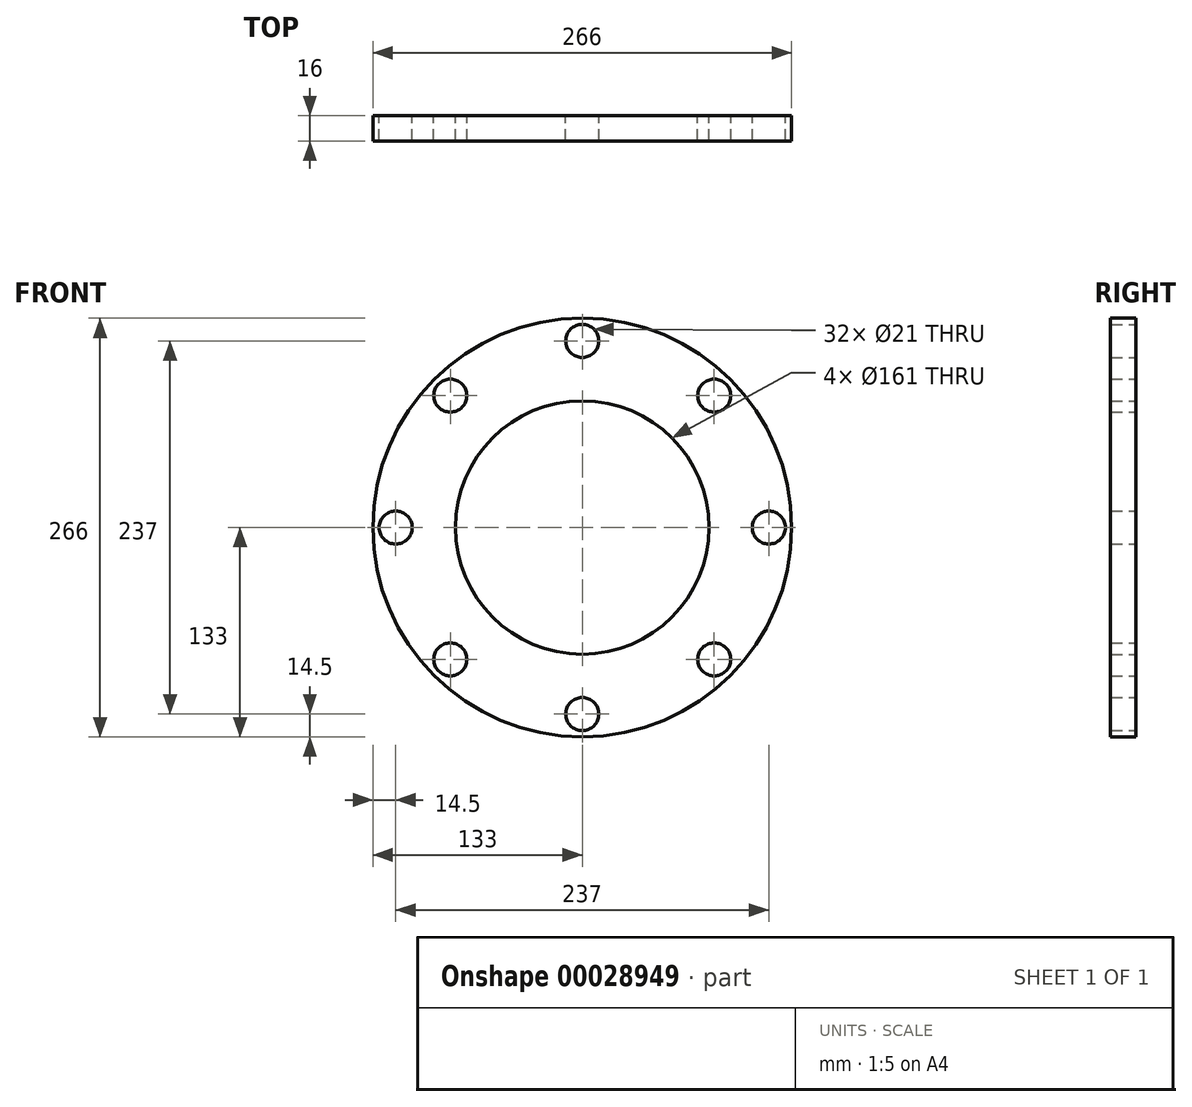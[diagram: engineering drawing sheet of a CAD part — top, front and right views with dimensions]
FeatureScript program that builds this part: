
annotation { "Feature Type Name" : "Feature", "Feature Type Description" : "" }
export const myFeature = defineFeature(function(context is Context, id is Id, definition is map)
    precondition{}
    {
        {
            var Q0;
            Q0=qCreatedBy(makeId("Front.planeOp"),FACE);
            var sketch = newSketch(context, id + "F0", { "sketchPlane" : qUnion([Q0])});
            skCircle(sketch, "E0", {"center": v(0, 0) * mm, "radius": 133 * mm});
            skCircle(sketch, "E1", {"center": v(0, 0) * mm, "radius": 80.5 * mm});
            skCircle(sketch, "E2", {"center": v(0, 0) * mm, "radius": 118.5 * mm, "construction": true});
            skCircle(sketch, "E3", {"center": v(0, 118.5) * mm, "radius": 10.5 * mm});
            skCircle(sketch, "E4.1.0", {"center": v(-83.8, 83.8) * mm, "radius": 10.5 * mm});
            skCircle(sketch, "E4.2.0", {"center": v(-118.5, 0) * mm, "radius": 10.5 * mm});
            skCircle(sketch, "E5.1.3.0", {"center": v(-83.8, -83.8) * mm, "radius": 10.5 * mm});
            skCircle(sketch, "E5.1.4.0", {"center": v(0, -118.5) * mm, "radius": 10.5 * mm});
            skCircle(sketch, "E5.1.5.0", {"center": v(83.8, -83.8) * mm, "radius": 10.5 * mm});
            skCircle(sketch, "E5.1.6.0", {"center": v(118.5, 0) * mm, "radius": 10.5 * mm});
            skCircle(sketch, "E5.1.7.0", {"center": v(83.8, 83.8) * mm, "radius": 10.5 * mm});
            skSolve(sketch);
        }
        {
            var Q0;
            Q0=makeQuery(id+"F0.imprint","IMPRINT",FACE,{"disambiguationData":[TD([[makeQuery(id+"F0.imprint","IMPRINT",EDGE,{"derivedFrom":sQuery(id+"F0.wireOp",EDGE,"E0")}),1.0]])]});
            extrude(context, id + "F1", {"entities" : qUnion([Q0]), "depth" : 16 * mm});
        }
    });
